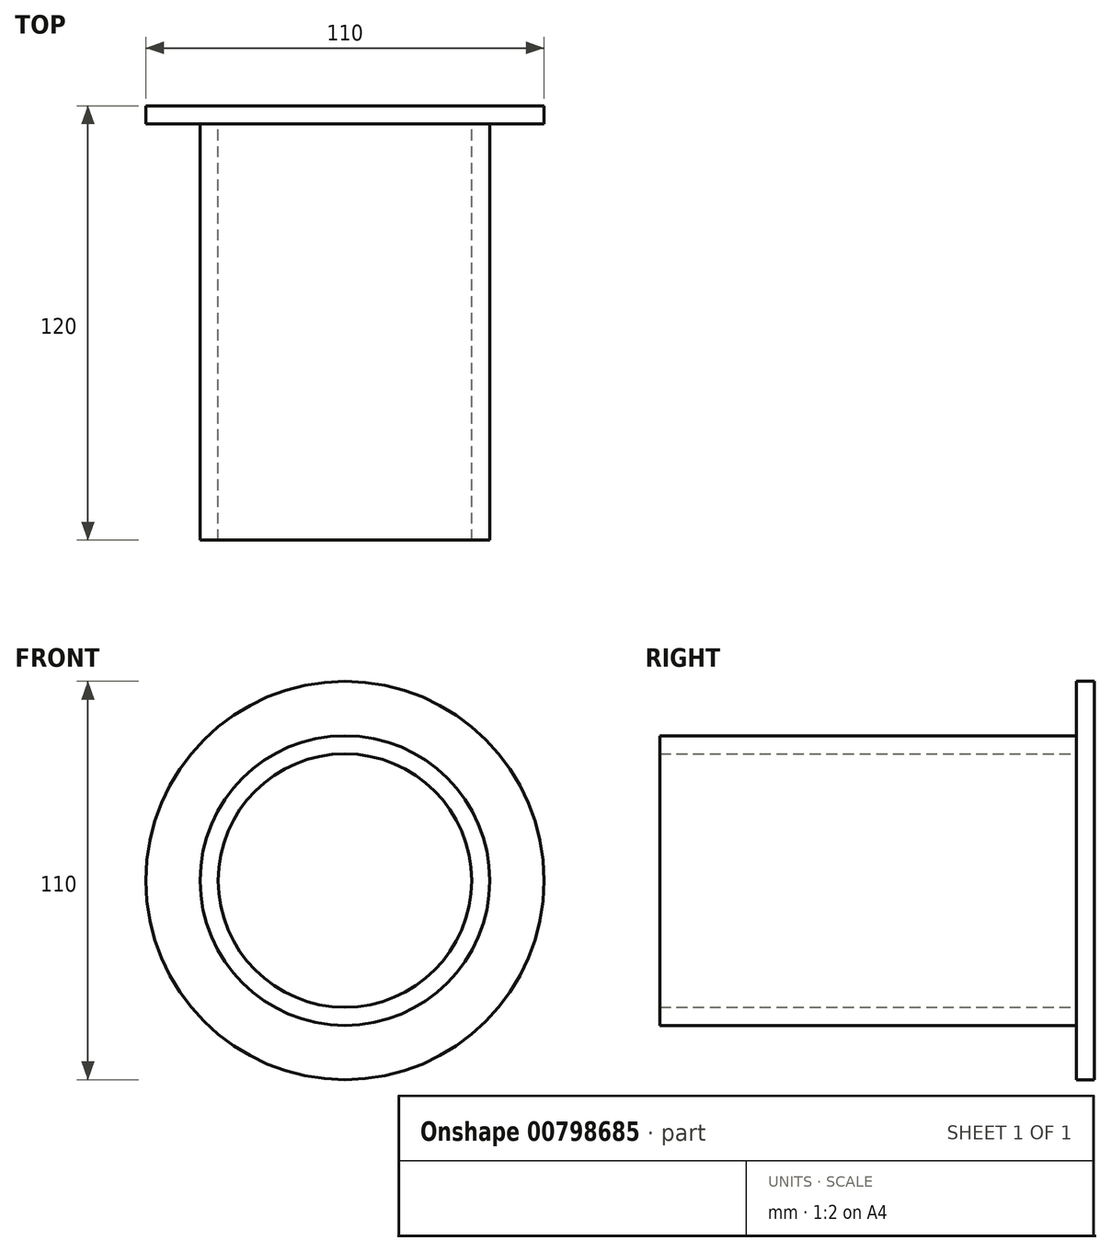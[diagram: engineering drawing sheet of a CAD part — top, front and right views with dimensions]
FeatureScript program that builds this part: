
annotation { "Feature Type Name" : "Feature", "Feature Type Description" : "" }
export const myFeature = defineFeature(function(context is Context, id is Id, definition is map)
    precondition{}
    {
        {
            var Q0;
            Q0=qCreatedBy(makeId("Front.planeOp"),FACE);
            var sketch = newSketch(context, id + "F0", { "sketchPlane" : qUnion([Q0])});
            skCircle(sketch, "E0", {"center": v(0, 0) * mm, "radius": 40 * mm});
            skCircle(sketch, "E1", {"center": v(0, 0) * mm, "radius": 35 * mm});
            skSolve(sketch);
        }
        {
            var Q0;
            Q0=makeQuery(id+"F0.imprint","IMPRINT",FACE,{"disambiguationData":[TD([[makeQuery(id+"F0.imprint","IMPRINT",EDGE,{"derivedFrom":sQuery(id+"F0.wireOp",EDGE,"E0")}),1.0]])]});
            extrude(context, id + "F1", {"entities" : qUnion([Q0]), "depth" : 120 * mm, "offsetDistance" : 25 * mm});
        }
        {
            var Q0;
            Q0=makeQuery(id+"F1.opExtrude","CAP_FACE",FACE,{"disambiguationData":[OSD([sQuery(id+"F0.wireOp",EDGE,"E0"),sQuery(id+"F0.wireOp",EDGE,"E1")])],"isStart":true});
            var sketch = newSketch(context, id + "F2", { "sketchPlane" : qUnion([Q0])});
            skCircle(sketch, "E2", {"center": v(0, 0) * mm, "radius": 55 * mm});
            skSolve(sketch);
        }
        {
            var Q0;
            Q0=makeQuery(id+"F2.imprint","IMPRINT",FACE,{"disambiguationData":[TD([[makeQuery(id+"F2.imprint","IMPRINT",EDGE,{"derivedFrom":sQuery(id+"F2.wireOp",EDGE,"E2")}),1.0]])]});
            var Q1;
            Q1=makeQuery(id+"F2.imprint","IMPRINT",FACE,{"disambiguationData":[TD([[makeQuery(id+"F2.imprint","IMPRINT",EDGE,{"derivedFrom":makeQuery(id+"F1.opExtrude","CAP_EDGE",EDGE,{"disambiguationData":[OSD([sQuery(id+"F0.wireOp",EDGE,"E0")])],"isStart":true})}),-1.0]])]});
            var Q2;
            Q2=makeQuery(id+"F2.imprint","IMPRINT",FACE,{"disambiguationData":[TD([[makeQuery(id+"F2.imprint","IMPRINT",EDGE,{"derivedFrom":makeQuery(id+"F1.opExtrude","CAP_EDGE",EDGE,{"disambiguationData":[OSD([sQuery(id+"F0.wireOp",EDGE,"E1")])],"isStart":true})}),-1.0]])]});
            extrude(context, id + "F3", {"entities" : qUnion([Q0, Q1, Q2]), "operationType" : NewBodyOperationType.ADD, "oppositeDirection" : true, "depth" : 5 * mm, "offsetDistance" : 25 * mm});
        }
    });
